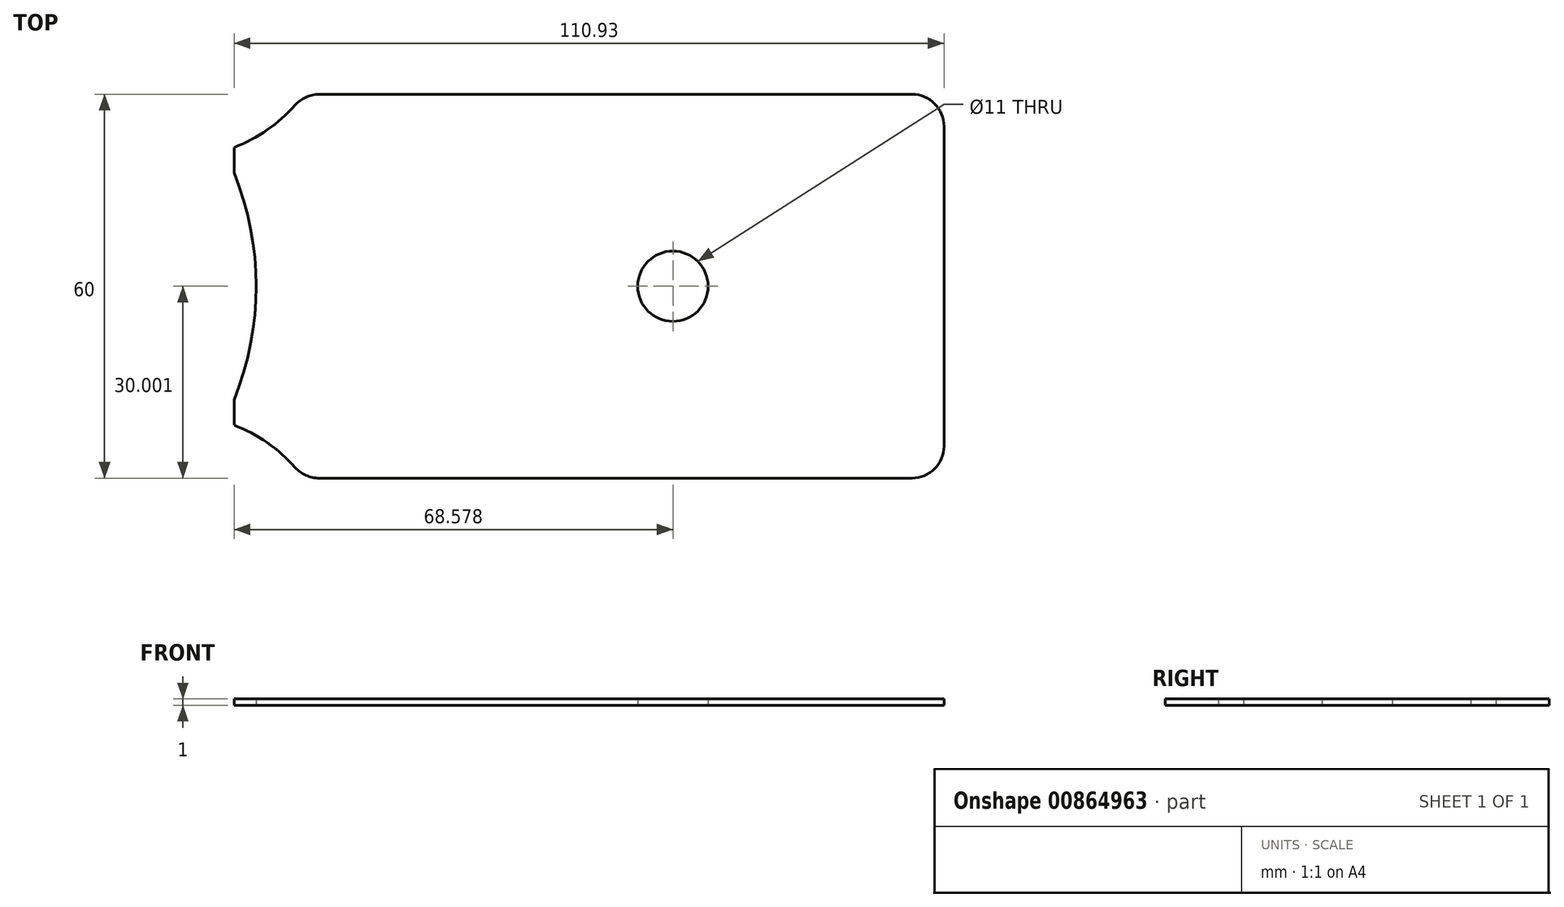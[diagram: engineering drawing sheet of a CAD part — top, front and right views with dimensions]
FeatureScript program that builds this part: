
annotation { "Feature Type Name" : "Feature", "Feature Type Description" : "" }
export const myFeature = defineFeature(function(context is Context, id is Id, definition is map)
    precondition{}
    {
        {
            var Q0;
            Q0=qCreatedBy(makeId("Top.planeOp"),FACE);
            var sketch = newSketch(context, id + "F0", { "sketchPlane" : qUnion([Q0])});
            skArc(sketch, "E0.0.0", {"start": v(-44.37, 8.86) * mm, "mid": v(-46.41, 8.43) * mm, "end": v(-48.1, 7.2) * mm});
            skArc(sketch, "E0.0.1", {"start": v(-48.1, 7.2) * mm, "mid": v(-52.49, 3.32) * mm, "end": v(-57.66, 0.57) * mm});
            skLineSegment(sketch, "E0.0.2", {"start": v(-57.66, 0.57) * mm, "end": v(-57.66, -3.38) * mm});
            skArc(sketch, "E0.0.3", {"start": v(-57.66, -3.38) * mm, "mid": v(-54.22, -21.14) * mm, "end": v(-57.66, -38.9) * mm});
            skLineSegment(sketch, "E0.0.4", {"start": v(-57.66, -38.9) * mm, "end": v(-57.66, -42.84) * mm});
            skArc(sketch, "E0.0.5", {"start": v(-57.66, -42.84) * mm, "mid": v(-52.49, -45.6) * mm, "end": v(-48.1, -49.47) * mm});
            skArc(sketch, "E0.0.6", {"start": v(-48.1, -49.47) * mm, "mid": v(-46.41, -50.7) * mm, "end": v(-44.37, -51.14) * mm});
            skLineSegment(sketch, "E0.0.7", {"start": v(-44.37, -51.14) * mm, "end": v(48.27, -51.14) * mm});
            skArc(sketch, "E0.0.8", {"start": v(48.27, -51.14) * mm, "mid": v(51.8, -49.67) * mm, "end": v(53.27, -46.14) * mm});
            skLineSegment(sketch, "E0.0.9", {"start": v(53.27, -46.14) * mm, "end": v(53.27, -22.44) * mm});
            skLineSegment(sketch, "E0.0.10", {"start": v(53.27, -22.44) * mm, "end": v(46.78, -22.44) * mm});
            skArc(sketch, "E0.0.11", {"start": v(46.78, -22.44) * mm, "mid": v(45.64, -22.8) * mm, "end": v(44.9, -23.75) * mm});
            skArc(sketch, "E0.0.12", {"start": v(44.9, -23.75) * mm, "mid": v(37.77, -28.74) * mm, "end": v(30.63, -23.75) * mm});
            skArc(sketch, "E0.0.13", {"start": v(30.63, -23.75) * mm, "mid": v(29.9, -22.8) * mm, "end": v(28.75, -22.44) * mm});
            skLineSegment(sketch, "E0.0.14", {"start": v(28.75, -22.44) * mm, "end": v(22.27, -22.44) * mm});
            skLineSegment(sketch, "E0.0.15", {"start": v(22.27, -22.44) * mm, "end": v(22.27, -36.14) * mm});
            skLineSegment(sketch, "E0.0.16", {"start": v(22.27, -36.14) * mm, "end": v(11.84, -36.14) * mm});
            skLineSegment(sketch, "E0.0.17", {"start": v(11.84, -36.14) * mm, "end": v(11.84, -38.44) * mm});
            skArc(sketch, "E0.0.18", {"start": v(11.84, -38.44) * mm, "mid": v(7.16, -42.75) * mm, "end": v(2.84, -38.07) * mm});
            skLineSegment(sketch, "E0.0.19", {"start": v(2.84, -38.07) * mm, "end": v(2.84, -36.14) * mm});
            skLineSegment(sketch, "E0.0.20", {"start": v(2.84, -36.14) * mm, "end": v(-22.3, -36.14) * mm});
            skLineSegment(sketch, "E0.0.21", {"start": v(-22.3, -36.14) * mm, "end": v(-22.3, -38.07) * mm});
            skArc(sketch, "E0.0.22", {"start": v(-22.3, -38.07) * mm, "mid": v(-26.62, -42.75) * mm, "end": v(-31.3, -38.44) * mm});
            skLineSegment(sketch, "E0.0.23", {"start": v(-31.3, -38.44) * mm, "end": v(-31.3, -36.14) * mm});
            skLineSegment(sketch, "E0.0.24", {"start": v(-31.3, -36.14) * mm, "end": v(-41.73, -36.14) * mm});
            skLineSegment(sketch, "E0.0.25", {"start": v(-41.73, -36.14) * mm, "end": v(-41.73, -6.14) * mm});
            skLineSegment(sketch, "E0.0.26", {"start": v(-41.73, -6.14) * mm, "end": v(-31.3, -6.14) * mm});
            skLineSegment(sketch, "E0.0.27", {"start": v(-31.3, -6.14) * mm, "end": v(-31.3, -3.84) * mm});
            skArc(sketch, "E0.0.28", {"start": v(-31.3, -3.84) * mm, "mid": v(-26.62, 0.47) * mm, "end": v(-22.3, -4.21) * mm});
            skLineSegment(sketch, "E0.0.29", {"start": v(-22.3, -4.21) * mm, "end": v(-22.3, -6.14) * mm});
            skLineSegment(sketch, "E0.0.30", {"start": v(-22.3, -6.14) * mm, "end": v(2.84, -6.14) * mm});
            skLineSegment(sketch, "E0.0.31", {"start": v(2.84, -6.14) * mm, "end": v(2.84, -4.21) * mm});
            skArc(sketch, "E0.0.32", {"start": v(2.84, -4.21) * mm, "mid": v(7.16, 0.47) * mm, "end": v(11.84, -3.84) * mm});
            skLineSegment(sketch, "E0.0.33", {"start": v(11.84, -3.84) * mm, "end": v(11.84, -6.14) * mm});
            skLineSegment(sketch, "E0.0.34", {"start": v(11.84, -6.14) * mm, "end": v(22.27, -6.14) * mm});
            skLineSegment(sketch, "E0.0.35", {"start": v(22.27, -6.14) * mm, "end": v(22.27, -19.84) * mm});
            skLineSegment(sketch, "E0.0.36", {"start": v(22.27, -19.84) * mm, "end": v(28.75, -19.84) * mm});
            skArc(sketch, "E0.0.37", {"start": v(28.75, -19.84) * mm, "mid": v(29.9, -19.48) * mm, "end": v(30.63, -18.53) * mm});
            skArc(sketch, "E0.0.38", {"start": v(30.63, -18.53) * mm, "mid": v(37.77, -13.54) * mm, "end": v(44.9, -18.53) * mm});
            skArc(sketch, "E0.0.39", {"start": v(44.9, -18.53) * mm, "mid": v(45.64, -19.48) * mm, "end": v(46.78, -19.84) * mm});
            skLineSegment(sketch, "E0.0.40", {"start": v(46.78, -19.84) * mm, "end": v(53.27, -19.84) * mm});
            skLineSegment(sketch, "E0.0.41", {"start": v(53.27, -19.84) * mm, "end": v(53.27, 3.86) * mm});
            skArc(sketch, "E0.0.42", {"start": v(53.27, 3.86) * mm, "mid": v(51.8, 7.4) * mm, "end": v(48.27, 8.86) * mm});
            skLineSegment(sketch, "E0.0.43", {"start": v(48.27, 8.86) * mm, "end": v(-44.37, 8.86) * mm});
            skCircle(sketch, "E1.0", {"center": v(37.77, -42.84) * mm, "radius": 1.25 * mm});
            skArc(sketch, "E2.0", {"start": v(42.01, -44.73) * mm, "mid": v(37.77, -38.19) * mm, "end": v(33.52, -44.73) * mm});
            skCircle(sketch, "E3.0", {"center": v(37.77, -21.14) * mm, "radius": 5 * mm});
            skCircle(sketch, "E4.0", {"center": v(-38.38, 0.56) * mm, "radius": 1.25 * mm});
            skCircle(sketch, "E5.0", {"center": v(-38.38, -42.84) * mm, "radius": 1.25 * mm});
            skCircle(sketch, "E6.0", {"center": v(37.77, 0.56) * mm, "radius": 1.25 * mm});
            skLineSegment(sketch, "E7", {"start": v(22.27, -19.84) * mm, "end": v(22.27, -22.44) * mm});
            skLineSegment(sketch, "E8", {"start": v(22.27, -21.14) * mm, "end": v(10.92, -21.14) * mm});
            skCircle(sketch, "E9", {"center": v(10.92, -21.14) * mm, "radius": 5.5 * mm});
            skLineSegment(sketch, "E10", {"start": v(53.27, -19.84) * mm, "end": v(53.27, -22.44) * mm});
            skSolve(sketch);
        }
        {
            var Q0;
            Q0=makeQuery(id+"F0.imprint","IMPRINT",FACE,{"disambiguationData":[TD([[makeQuery(id+"F0.imprint","IMPRINT",EDGE,{"derivedFrom":sQuery(id+"F0.wireOp",EDGE,"E0.0.0")}),1.0]])]});
            var Q1;
            {var subQ3=sQuery(id+"F0.wireOp",EDGE,"E0.0.15");Q1=makeQuery(id+"F0.imprint","IMPRINT",FACE,{"disambiguationData":[TD([[makeQuery(id+"F0.imprint","IMPRINT",EDGE,{"derivedFrom":subQ3}),-1.0]])]});}
            var Q2;
            Q2=makeQuery(id+"F0.imprint","IMPRINT",FACE,{"disambiguationData":[TD([[makeQuery(id+"F0.imprint","IMPRINT",EDGE,{"derivedFrom":sQuery(id+"F0.wireOp",EDGE,"E0.0.10")}),-1.0]])]});
            var Q3;
            Q3=makeQuery(id+"F0.imprint","IMPRINT",FACE,{"disambiguationData":[TD([[makeQuery(id+"F0.imprint","IMPRINT",EDGE,{"derivedFrom":sQuery(id+"F0.wireOp",EDGE,"E3.0")}),1.0]])]});
            var Q4;
            Q4=makeQuery(id+"F0.imprint","IMPRINT",FACE,{"disambiguationData":[TD([[makeQuery(id+"F0.imprint","IMPRINT",EDGE,{"derivedFrom":sQuery(id+"F0.wireOp",EDGE,"E6.0")}),1.0]])]});
            var Q5;
            Q5=makeQuery(id+"F0.imprint","IMPRINT",FACE,{"disambiguationData":[TD([[makeQuery(id+"F0.imprint","IMPRINT",EDGE,{"derivedFrom":sQuery(id+"F0.wireOp",EDGE,"E1.0")}),1.0]])]});
            var Q6;
            Q6=makeQuery(id+"F0.imprint","IMPRINT",FACE,{"disambiguationData":[TD([[makeQuery(id+"F0.imprint","IMPRINT",EDGE,{"derivedFrom":sQuery(id+"F0.wireOp",EDGE,"E5.0")}),1.0]])]});
            var Q7;
            Q7=makeQuery(id+"F0.imprint","IMPRINT",FACE,{"disambiguationData":[TD([[makeQuery(id+"F0.imprint","IMPRINT",EDGE,{"derivedFrom":sQuery(id+"F0.wireOp",EDGE,"E4.0")}),1.0]])]});
            extrude(context, id + "F1", {"entities" : qUnion([Q0, Q1, Q2, Q3, Q4, Q5, Q6, Q7]), "depth" : 1 * mm, "offsetDistance" : 25 * mm});
        }
    });
